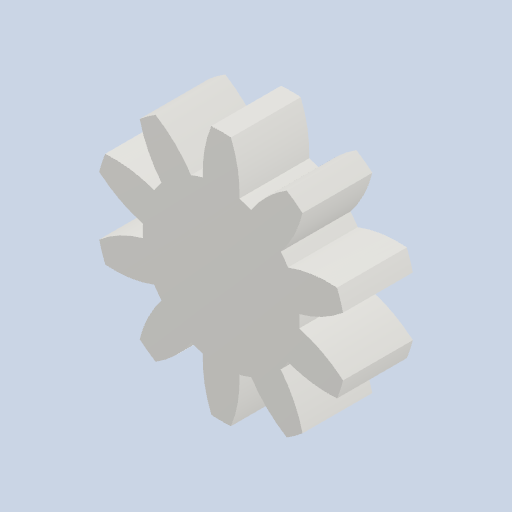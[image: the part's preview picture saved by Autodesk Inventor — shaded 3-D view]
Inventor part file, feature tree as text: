
AUTODESK INVENTOR PART (.ipt)
format: ipt  version: 2022 (Build 260153000, 153)  size: 183,296 bytes
history: native  units: mm (DEFAULTED — no unit token found)
features: plane x3, other x3, sketch x2, extrude x1
ambient origin geometry x8: Origin, YZ Plane, XZ Plane, XY Plane, X Axis, Y Axis, Z Axis, Center Point
bodies: Solid1 (feature_tree)
feature tree (9):
  extrude  "Extrusion1"  Depth=5.0mm TaperAngle=0.0deg
  plane  "Work Plane2"
  plane  "Work Plane8"
  plane  "Work Plane9"
  other  "Цилиндрическое зубчатое зацепление"
  sketch  "Sketch1"  dims[d0=17.98627mm d1=5.0mm d2=0.0mm]
  sketch  "Sketch2"  dims[d3=15.0mm d4=10.0mm d5=0.0mm d16=38.516933mm d17=0.0mm d34=3.141593mm d39=0.0mm d41=0.0mm d43=38.516933mm d46=38.516933mm d47=0.0mm d48=0.0mm]
  other  "Srf1"
  other  "Средний диаметр"
